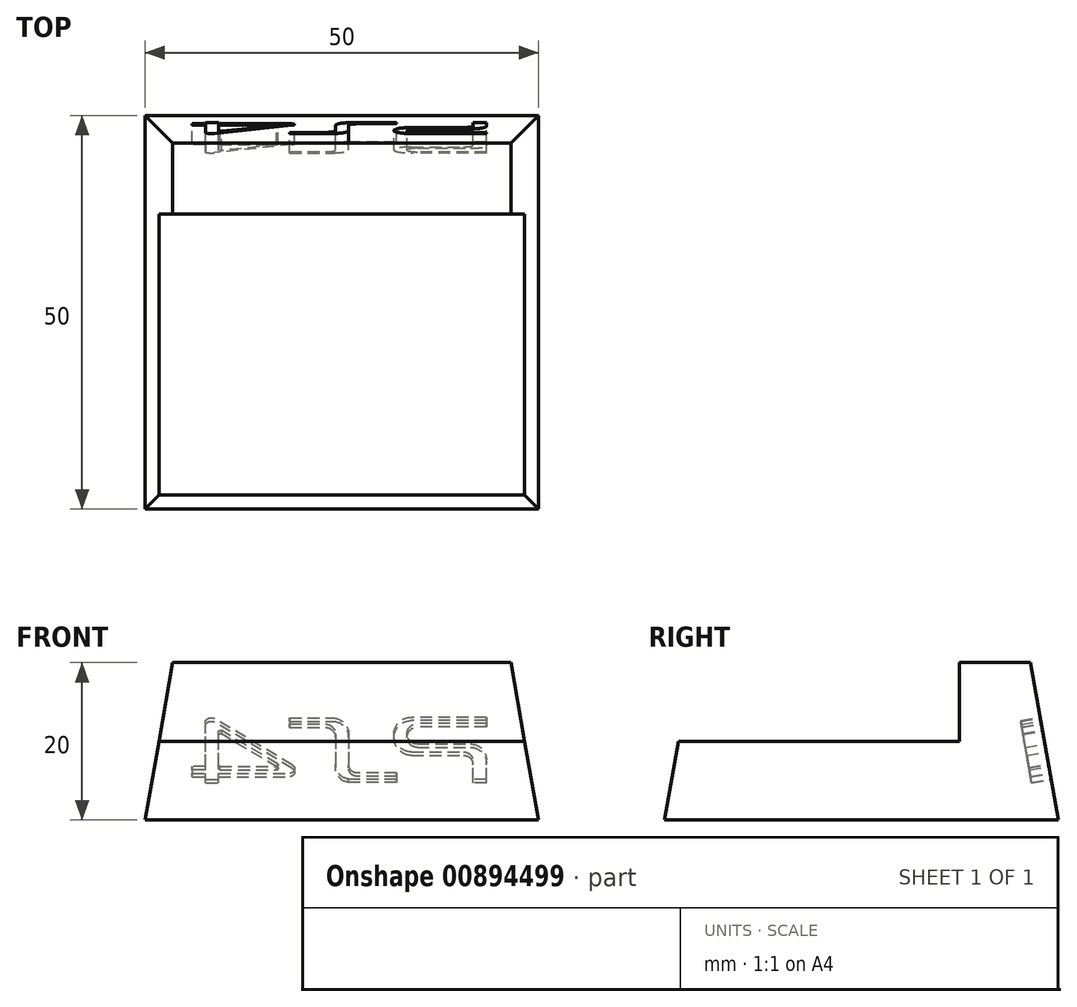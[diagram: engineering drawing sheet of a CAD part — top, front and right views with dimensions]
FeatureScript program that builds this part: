
annotation { "Feature Type Name" : "Feature", "Feature Type Description" : "" }
export const myFeature = defineFeature(function(context is Context, id is Id, definition is map)
    precondition{}
    {
        {
            var Q0;
            Q0=qCreatedBy(makeId("Top.planeOp"),FACE);
            var sketch = newSketch(context, id + "F0", { "sketchPlane" : qUnion([Q0])});
            skLineSegment(sketch, "E0.bottom", {"start": v(-25, 25) * mm, "end": v(25, 25) * mm});
            skLineSegment(sketch, "E0.top", {"start": v(-25, -25) * mm, "end": v(25, -25) * mm});
            skLineSegment(sketch, "E0.left", {"start": v(-25, 25) * mm, "end": v(-25, -25) * mm});
            skLineSegment(sketch, "E0.right", {"start": v(25, 25) * mm, "end": v(25, -25) * mm});
            skPoint(sketch, "E0.middle", {"position": v(0, 0) * mm});
            skSolve(sketch);
        }
        {
            var Q0;
            Q0=makeQuery(id+"F0.imprint","IMPRINT",FACE,{"disambiguationData":[TD([[makeQuery(id+"F0.imprint","IMPRINT",EDGE,{"derivedFrom":sQuery(id+"F0.wireOp",EDGE,"E0.bottom")}),-1.0]])]});
            extrude(context, id + "F1", {"entities" : qUnion([Q0]), "depth" : 20 * mm, "offsetDistance" : 25 * mm, "hasDraft" : true, "draftAngle" : 10 * degree, "draftPullDirection" : true});
        }
        {
            var Q0;
            Q0=makeQuery(id+"F1.opExtrude","SWEPT_FACE",FACE,{"disambiguationData":[OSD([sQuery(id+"F0.wireOp",EDGE,"E0.left")])]});
            var sketch = newSketch(context, id + "F2", { "sketchPlane" : qUnion([Q0])});
            skSolve(sketch);
        }
        {
            var Q0;
            Q0=makeQuery(id+"F1.opExtrude","SWEPT_FACE",FACE,{"disambiguationData":[OSD([sQuery(id+"F0.wireOp",EDGE,"E0.bottom")])]});
            var sketch = newSketch(context, id + "F3", { "sketchPlane" : qUnion([Q0])});
            skLineSegment(sketch, "E1", {"start": v(-67.7, 13.55) * mm, "end": v(-67.7, 1.7) * mm});
            skLineSegment(sketch, "E2", {"start": v(-67.7, 1.7) * mm, "end": v(-65, 0.65) * mm});
            skLineSegment(sketch, "E3", {"start": v(-63.86, 6.57) * mm, "end": v(-63.86, 10.9) * mm});
            skLineSegment(sketch, "E4", {"start": v(-64.35, 2.5) * mm, "end": v(-59.85, 4.13) * mm});
            skLineSegment(sketch, "E5", {"start": v(-64.37, 3.57) * mm, "end": v(-61.36, 4.65) * mm});
            skLineSegment(sketch, "E6", {"start": v(-64.35, 2.5) * mm, "end": v(-64.35, 0.9) * mm});
            skLineSegment(sketch, "E7", {"start": v(-64.35, 0.9) * mm, "end": v(-59.2, 2.75) * mm});
            skLineSegment(sketch, "E8", {"start": v(-64.37, 3.57) * mm, "end": v(-64.37, 5.16) * mm});
            skLineSegment(sketch, "E9", {"start": v(-64.37, 5.16) * mm, "end": v(-63.86, 5.34) * mm});
            skLineSegment(sketch, "E10", {"start": v(-68.23, 4.85) * mm, "end": v(-71.37, 3.72) * mm});
            skLineSegment(sketch, "E11", {"start": v(-68.23, 4.85) * mm, "end": v(-68.23, 6.4) * mm});
            skLineSegment(sketch, "E12", {"start": v(-68.23, 6.4) * mm, "end": v(-72.86, 4.73) * mm});
            skLineSegment(sketch, "E13", {"start": v(-68.23, 3.77) * mm, "end": v(-68.23, 2.32) * mm});
            skArc(sketch, "E14", {"start": v(-63.86, 10.9) * mm, "mid": v(-64.43, 11.47) * mm, "end": v(-65, 10.9) * mm});
            skLineSegment(sketch, "E15", {"start": v(-65, 0.65) * mm, "end": v(-65, 10.9) * mm});
            skArc(sketch, "E16", {"start": v(-62.61, 12.05) * mm, "mid": v(-65.1, 12.96) * mm, "end": v(-67.7, 13.55) * mm});
            skArc(sketch, "E17", {"start": v(-60.93, 9.9) * mm, "mid": v(-61.5, 11.19) * mm, "end": v(-62.61, 12.05) * mm});
            skArc(sketch, "E18", {"start": v(-60.93, 7.36) * mm, "mid": v(-60.81, 8.63) * mm, "end": v(-60.93, 9.9) * mm});
            skArc(sketch, "E19", {"start": v(-62.36, 6.18) * mm, "mid": v(-61.5, 6.59) * mm, "end": v(-60.93, 7.36) * mm});
            skArc(sketch, "E20", {"start": v(-63.86, 6.57) * mm, "mid": v(-63.16, 6.2) * mm, "end": v(-62.36, 6.18) * mm});
            skArc(sketch, "E21", {"start": v(-60.8, 5.66) * mm, "mid": v(-62.34, 5.61) * mm, "end": v(-63.86, 5.34) * mm});
            skArc(sketch, "E22", {"start": v(-57.57, 4.85) * mm, "mid": v(-59.14, 5.45) * mm, "end": v(-60.8, 5.66) * mm});
            skArc(sketch, "E23", {"start": v(-57.13, 4.28) * mm, "mid": v(-57.27, 4.63) * mm, "end": v(-57.57, 4.85) * mm});
            skArc(sketch, "E24", {"start": v(-57.57, 3.53) * mm, "mid": v(-57.21, 3.83) * mm, "end": v(-57.13, 4.28) * mm});
            skArc(sketch, "E25", {"start": v(-59.2, 2.75) * mm, "mid": v(-58.36, 3.1) * mm, "end": v(-57.57, 3.53) * mm});
            skArc(sketch, "E26", {"start": v(-60.08, 4.73) * mm, "mid": v(-60.82, 4.77) * mm, "end": v(-61.54, 4.59) * mm});
            skArc(sketch, "E27", {"start": v(-59.63, 4.48) * mm, "mid": v(-59.83, 4.65) * mm, "end": v(-60.08, 4.73) * mm});
            skArc(sketch, "E28", {"start": v(-59.63, 4.3) * mm, "mid": v(-59.6, 4.39) * mm, "end": v(-59.63, 4.48) * mm});
            skArc(sketch, "E29", {"start": v(-59.85, 4.13) * mm, "mid": v(-59.73, 4.2) * mm, "end": v(-59.63, 4.3) * mm});
            skPoint(sketch, "E30.orphan", {"position": v(-62.36, 5.88) * mm});
            skPoint(sketch, "E31.orphan", {"position": v(-60.8, 4.85) * mm});
            skPoint(sketch, "E32.orphan", {"position": v(-59.42, 4.28) * mm});
            skArc(sketch, "E33", {"start": v(-72.86, 4.73) * mm, "mid": v(-73.37, 4.42) * mm, "end": v(-73.8, 4) * mm});
            skArc(sketch, "E34", {"start": v(-73.8, 4) * mm, "mid": v(-73.85, 3.72) * mm, "end": v(-73.8, 3.44) * mm});
            skArc(sketch, "E35", {"start": v(-73.8, 3.44) * mm, "mid": v(-73.57, 3.08) * mm, "end": v(-73.2, 2.87) * mm});
            skArc(sketch, "E36", {"start": v(-73.2, 2.87) * mm, "mid": v(-72.7, 2.63) * mm, "end": v(-72.15, 2.5) * mm});
            skArc(sketch, "E37", {"start": v(-72.15, 2.5) * mm, "mid": v(-71.02, 2.26) * mm, "end": v(-69.87, 2.2) * mm});
            skArc(sketch, "E38", {"start": v(-69.87, 2.2) * mm, "mid": v(-69.05, 2.22) * mm, "end": v(-68.23, 2.32) * mm});
            skArc(sketch, "E39", {"start": v(-69.2, 3.44) * mm, "mid": v(-68.71, 3.58) * mm, "end": v(-68.23, 3.77) * mm});
            skArc(sketch, "E40", {"start": v(-71.37, 3.26) * mm, "mid": v(-70.27, 3.15) * mm, "end": v(-69.2, 3.44) * mm});
            skArc(sketch, "E41", {"start": v(-71.37, 3.72) * mm, "mid": v(-71.47, 3.49) * mm, "end": v(-71.37, 3.26) * mm});
            skLineSegment(sketch, "E42", {"start": v(-18.37, 8.93) * mm, "end": v(-8.86, 8.93) * mm});
            skLineSegment(sketch, "E43", {"start": v(-18.37, 8.93) * mm, "end": v(-18.37, 8.1) * mm});
            skLineSegment(sketch, "E44", {"start": v(-18.37, 8.1) * mm, "end": v(-9.61, 8.1) * mm});
            skLineSegment(sketch, "E45", {"start": v(-9.61, 5.46) * mm, "end": v(-16.37, 5.46) * mm});
            skLineSegment(sketch, "E46", {"start": v(-18.37, 0.9) * mm, "end": v(-18.37, 3.45) * mm});
            skLineSegment(sketch, "E47", {"start": v(-18.37, 0.9) * mm, "end": v(-16.67, 0.9) * mm});
            skLineSegment(sketch, "E48", {"start": v(-16.67, 0.9) * mm, "end": v(-16.67, 3.25) * mm});
            skLineSegment(sketch, "E49", {"start": v(-8.86, 4.44) * mm, "end": v(-15.48, 4.44) * mm});
            skLineSegment(sketch, "E50", {"start": v(6.63, 8.84) * mm, "end": v(1.2, 8.84) * mm});
            skLineSegment(sketch, "E51", {"start": v(6.63, 8.84) * mm, "end": v(6.63, 8.03) * mm});
            skLineSegment(sketch, "E52", {"start": v(6.63, 8.03) * mm, "end": v(2.07, 8.03) * mm});
            skLineSegment(sketch, "E53", {"start": v(0.8, 6.76) * mm, "end": v(0.8, 2.85) * mm});
            skLineSegment(sketch, "E54", {"start": v(-0.87, 6.76) * mm, "end": v(-0.87, 2.8) * mm});
            skLineSegment(sketch, "E55", {"start": v(-6.95, 1.74) * mm, "end": v(-1.92, 1.74) * mm});
            skLineSegment(sketch, "E56", {"start": v(-6.95, 1.74) * mm, "end": v(-6.95, 0.92) * mm});
            skLineSegment(sketch, "E57", {"start": v(-6.95, 0.92) * mm, "end": v(-0.87, 0.92) * mm});
            skLineSegment(sketch, "E58", {"start": v(6.3, 2.77) * mm, "end": v(16.15, 8.73) * mm});
            skLineSegment(sketch, "E59", {"start": v(15.48, 2.58) * mm, "end": v(8.2, 2.58) * mm});
            skLineSegment(sketch, "E60", {"start": v(15.63, 2.77) * mm, "end": v(15.63, 7.12) * mm});
            skLineSegment(sketch, "E61", {"start": v(17.3, 0.89) * mm, "end": v(17.3, 1.68) * mm});
            skLineSegment(sketch, "E62", {"start": v(17.3, 0.89) * mm, "end": v(15.63, 0.89) * mm});
            skLineSegment(sketch, "E63", {"start": v(15.63, 0.89) * mm, "end": v(15.63, 1.68) * mm});
            skLineSegment(sketch, "E64", {"start": v(17.3, 2.58) * mm, "end": v(19, 2.58) * mm});
            skLineSegment(sketch, "E65", {"start": v(19, 2.58) * mm, "end": v(19, 1.68) * mm});
            skLineSegment(sketch, "E66", {"start": v(19, 1.68) * mm, "end": v(17.3, 1.68) * mm});
            skArc(sketch, "E67", {"start": v(-9.61, 5.46) * mm, "mid": v(-8.3, 6.78) * mm, "end": v(-9.61, 8.1) * mm});
            skArc(sketch, "E68", {"start": v(-16.37, 5.46) * mm, "mid": v(-17.78, 4.87) * mm, "end": v(-18.37, 3.45) * mm});
            skArc(sketch, "E69", {"start": v(-15.48, 4.44) * mm, "mid": v(-16.32, 4.1) * mm, "end": v(-16.67, 3.25) * mm});
            skArc(sketch, "E70", {"start": v(-8.86, 4.44) * mm, "mid": v(-6.61, 6.69) * mm, "end": v(-8.86, 8.93) * mm});
            skArc(sketch, "E71", {"start": v(1.2, 8.84) * mm, "mid": v(-0.26, 8.23) * mm, "end": v(-0.87, 6.76) * mm});
            skArc(sketch, "E72", {"start": v(2.07, 8.03) * mm, "mid": v(1.17, 7.66) * mm, "end": v(0.8, 6.76) * mm});
            skArc(sketch, "E73", {"start": v(-1.92, 1.74) * mm, "mid": v(-1.18, 2.05) * mm, "end": v(-0.87, 2.8) * mm});
            skArc(sketch, "E74", {"start": v(-1.13, 0.92) * mm, "mid": v(0.24, 1.49) * mm, "end": v(0.8, 2.85) * mm});
            skArc(sketch, "E75", {"start": v(6.3, 2.77) * mm, "mid": v(6.03, 2.11) * mm, "end": v(6.6, 1.68) * mm});
            skArc(sketch, "E76", {"start": v(17.3, 8.43) * mm, "mid": v(16.8, 8.82) * mm, "end": v(16.15, 8.73) * mm});
            skPoint(sketch, "E76.startSnap0", {"position": v(17.3, 5.53) * mm});
            skArc(sketch, "E77", {"start": v(8.17, 2.91) * mm, "mid": v(8.07, 2.69) * mm, "end": v(8.29, 2.58) * mm});
            skArc(sketch, "E78", {"start": v(15.48, 2.58) * mm, "mid": v(15.6, 2.66) * mm, "end": v(15.63, 2.8) * mm});
            skArc(sketch, "E79", {"start": v(15.63, 7.12) * mm, "mid": v(15.48, 7.24) * mm, "end": v(15.3, 7.21) * mm});
            skLineSegment(sketch, "E80.trimOffspring", {"start": v(-0.87, 0.94) * mm, "end": v(-0.87, 0.92) * mm});
            skLineSegment(sketch, "E81.trimOffspring", {"start": v(0.8, 0.92) * mm, "end": v(0.8, 0.76) * mm});
            skPoint(sketch, "E82.trimOffspring.end.orphan", {"position": v(3.1, 1.74) * mm});
            skPoint(sketch, "E83.orphan", {"position": v(0.8, 7.4) * mm});
            skPoint(sketch, "E84.orphan", {"position": v(0.8, 8.03) * mm});
            skLineSegment(sketch, "E85.trimOffspring", {"start": v(8.13, 2.89) * mm, "end": v(15.3, 7.21) * mm});
            skPoint(sketch, "E86.start.orphan", {"position": v(7.34, 2.41) * mm});
            skPoint(sketch, "E87.orphan", {"position": v(15.91, 2.58) * mm});
            skPoint(sketch, "E88.orphan", {"position": v(15.63, 2.41) * mm});
            skLineSegment(sketch, "E89.trimOffspring", {"start": v(17.3, 2.58) * mm, "end": v(17.3, 8.43) * mm});
            skLineSegment(sketch, "E90.trimOffspring", {"start": v(15.63, 1.68) * mm, "end": v(6.6, 1.68) * mm});
            skPoint(sketch, "E91.trimOffspring.end.orphan", {"position": v(15.63, 7.84) * mm});
            skPoint(sketch, "E92.trimOffspring.end.orphan", {"position": v(17.3, 10.17) * mm});
            skLineSegment(sketch, "E93", {"start": v(-0.87, 10.41) * mm, "end": v(6.63, 10.41) * mm});
            skSolve(sketch);
        }
        {
            var Q0;
            Q0=qSketchRegion(id+"F3",true);
            extrude(context, id + "F4", {"entities" : qUnion([Q0]), "operationType" : NewBodyOperationType.REMOVE, "oppositeDirection" : true, "depth" : 2.5 * mm, "offsetDistance" : 25 * mm});
        }
        {
            var Q0;
            Q0=makeQuery(id+"F1.opExtrude","CAP_FACE",FACE,{"disambiguationData":[OSD([sQuery(id+"F0.wireOp",EDGE,"E0.bottom"),sQuery(id+"F0.wireOp",EDGE,"E0.top"),sQuery(id+"F0.wireOp",EDGE,"E0.left"),sQuery(id+"F0.wireOp",EDGE,"E0.right")])],"isStart":false});
            var sketch = newSketch(context, id + "F5", { "sketchPlane" : qUnion([Q0])});
            skLineSegment(sketch, "E94.bottom", {"start": v(-40, 12.47) * mm, "end": v(40, 12.47) * mm});
            skLineSegment(sketch, "E94.top", {"start": v(-40, -37.53) * mm, "end": v(40, -37.53) * mm});
            skLineSegment(sketch, "E94.left", {"start": v(-40, 12.47) * mm, "end": v(-40, -37.53) * mm});
            skLineSegment(sketch, "E94.right", {"start": v(40, 12.47) * mm, "end": v(40, -37.53) * mm});
            skPoint(sketch, "E95", {"position": v(0, -37.53) * mm});
            skSolve(sketch);
        }
        {
            var Q0;
            Q0=makeQuery(id+"F5.imprint","IMPRINT",FACE,{"disambiguationData":[TD([[makeQuery(id+"F5.imprint","IMPRINT",EDGE,{"derivedFrom":sQuery(id+"F5.wireOp",EDGE,"E94.top")}),1.0]])]});
            var Q1;
            {var subQ5=makeQuery(id+"F1.opExtrude","CAP_EDGE",EDGE,{"disambiguationData":[OSD([sQuery(id+"F0.wireOp",EDGE,"E0.top")])],"isStart":false});Q1=makeQuery(id+"F5.imprint","IMPRINT",FACE,{"disambiguationData":[TD([[makeQuery(id+"F5.imprint","IMPRINT",EDGE,{"derivedFrom":subQ5}),1.0]])]});}
            extrude(context, id + "F6", {"entities" : qUnion([Q0, Q1]), "operationType" : NewBodyOperationType.REMOVE, "oppositeDirection" : true, "depth" : 10 * mm, "offsetDistance" : 25 * mm});
        }
    });
